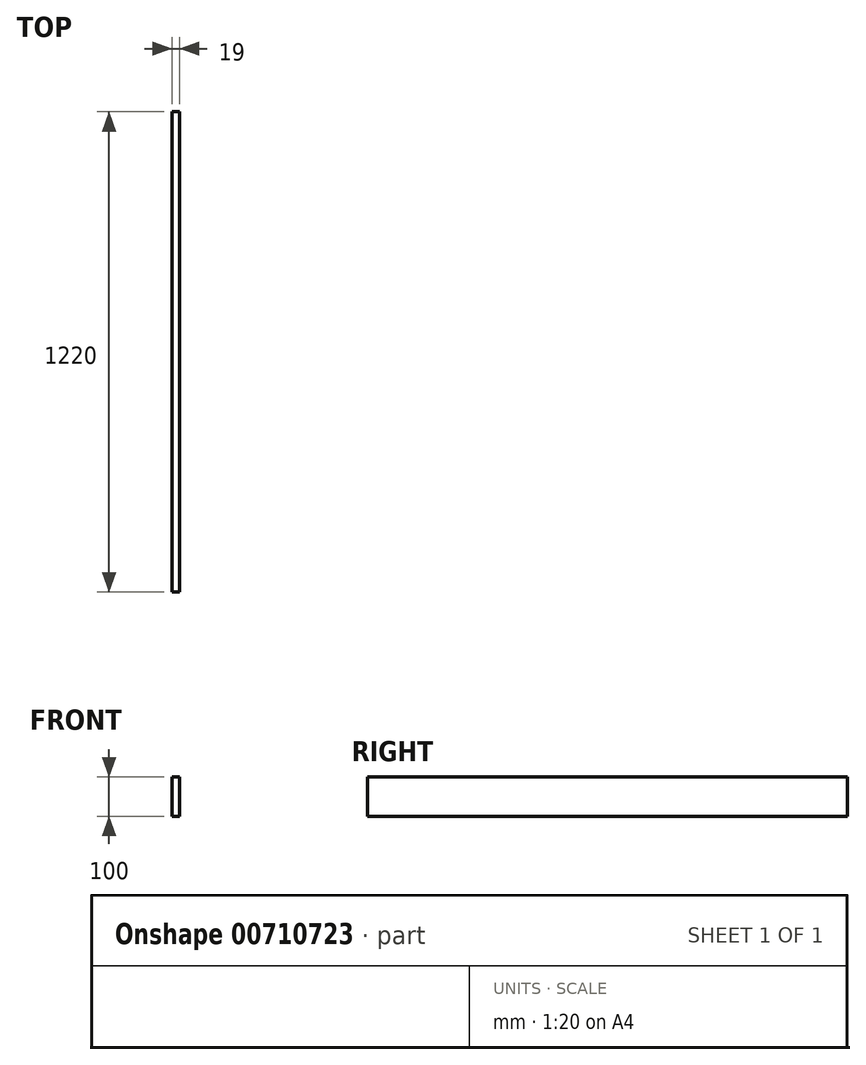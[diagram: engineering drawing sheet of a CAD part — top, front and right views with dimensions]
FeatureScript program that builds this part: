
annotation { "Feature Type Name" : "Feature", "Feature Type Description" : "" }
export const myFeature = defineFeature(function(context is Context, id is Id, definition is map)
    precondition{}
    {
        {
            var Q0;
            Q0=qCreatedBy(makeId("Front.planeOp"),FACE);
            var sketch = newSketch(context, id + "F0", { "sketchPlane" : qUnion([Q0])});
            skLineSegment(sketch, "E0.bottom", {"start": v(0, 0) * mm, "end": v(19, 0) * mm});
            skLineSegment(sketch, "E0.top", {"start": v(0, 100) * mm, "end": v(19, 100) * mm});
            skLineSegment(sketch, "E0.left", {"start": v(0, 0) * mm, "end": v(0, 100) * mm});
            skLineSegment(sketch, "E0.right", {"start": v(19, 0) * mm, "end": v(19, 100) * mm});
            skSolve(sketch);
        }
        {
            var Q0;
            Q0=qSketchRegion(id+"F0",true);
            extrude(context, id + "F1", {"entities" : qUnion([Q0]), "depth" : 1220 * mm, "offsetDistance" : 25 * mm});
        }
    });
